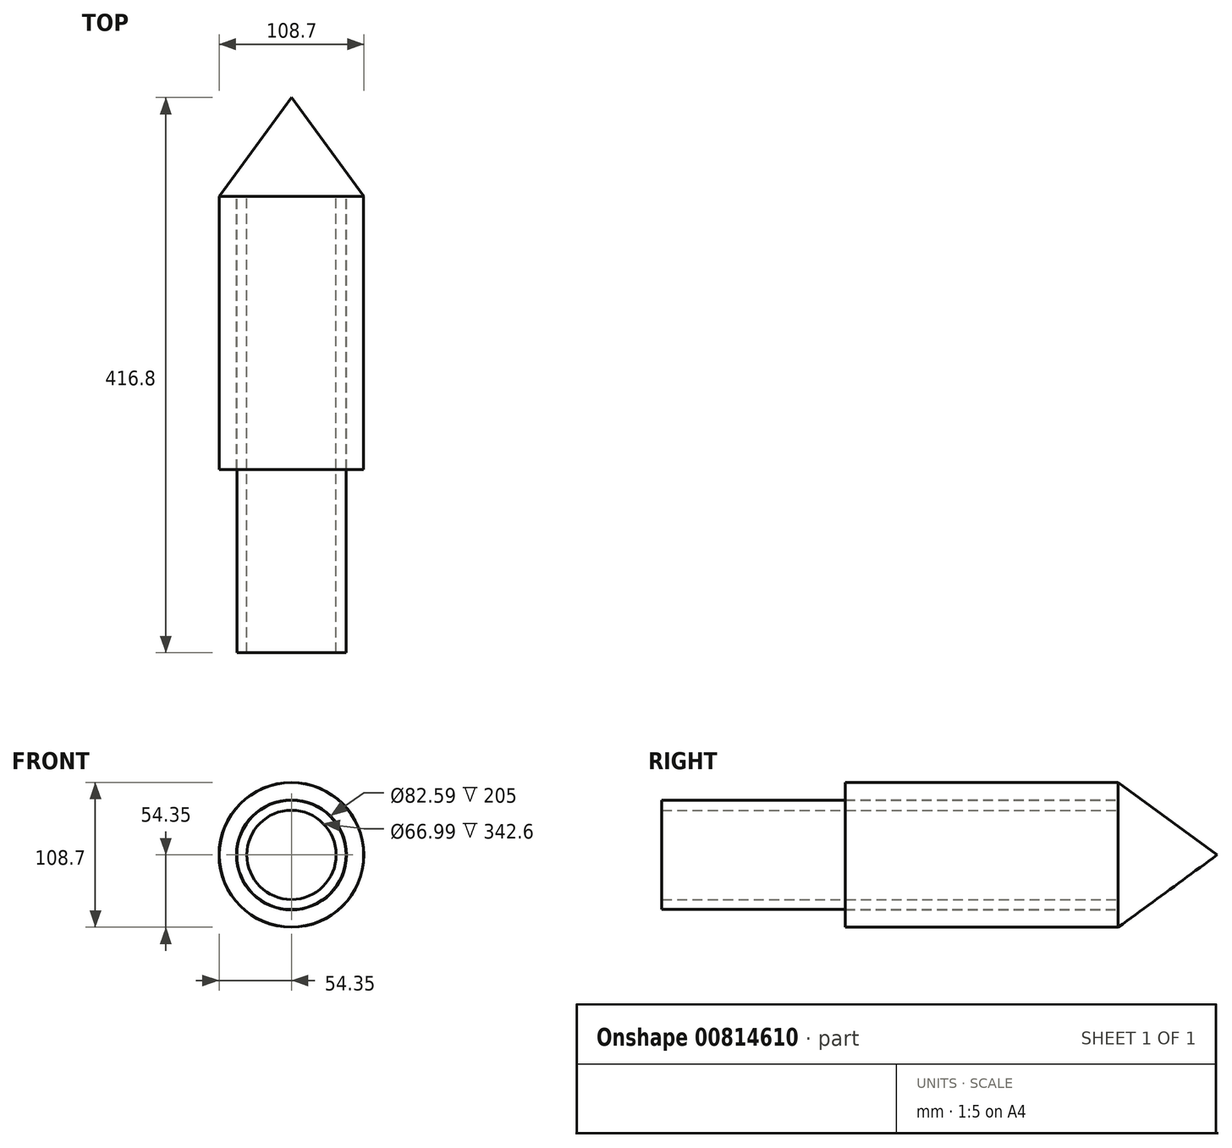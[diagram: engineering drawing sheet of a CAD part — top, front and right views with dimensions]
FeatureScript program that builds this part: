
annotation { "Feature Type Name" : "Feature", "Feature Type Description" : "" }
export const myFeature = defineFeature(function(context is Context, id is Id, definition is map)
    precondition{}
    {
        {
            var Q0;
            Q0=qCreatedBy(makeId("Front.planeOp"),FACE);
            var sketch = newSketch(context, id + "F0", { "sketchPlane" : qUnion([Q0])});
            skCircle(sketch, "E0", {"center": v(0, 0) * mm, "radius": 54.2 * mm});
            skCircle(sketch, "E1", {"center": v(0, 0) * mm, "radius": 41.3 * mm});
            skSolve(sketch);
        }
        {
            var Q0;
            Q0=makeQuery(id+"F0.imprint","IMPRINT",FACE,{"disambiguationData":[TD([[makeQuery(id+"F0.imprint","IMPRINT",EDGE,{"derivedFrom":sQuery(id+"F0.wireOp",EDGE,"E0")}),1.0]])]});
            extrude(context, id + "F1", {"entities" : qUnion([Q0]), "depth" : 205 * mm, "offsetDistance" : 25 * mm});
        }
        {
            var Q0;
            Q0=qCreatedBy(makeId("Right.planeOp"),FACE);
            var sketch = newSketch(context, id + "F2", { "sketchPlane" : qUnion([Q0])});
            skLineSegment(sketch, "E2", {"start": v(0, 0) * mm, "end": v(74.2, 0) * mm});
            skLineSegment(sketch, "E3", {"start": v(0, 0) * mm, "end": v(0, 54.35) * mm});
            skLineSegment(sketch, "E4", {"start": v(0, 54.35) * mm, "end": v(74.2, 0) * mm});
            skSolve(sketch);
        }
        {
            var Q0;
            Q0=makeQuery(id+"F2.imprint","IMPRINT",FACE,{"disambiguationData":[TD([[makeQuery(id+"F2.imprint","IMPRINT",EDGE,{"derivedFrom":sQuery(id+"F2.wireOp",EDGE,"E2")}),1.0]])]});
            var Q1;
            Q1=sQuery(id+"F2.wireOp",EDGE,"E2");
            revolve(context, id + "F3", {"operationType" : NewBodyOperationType.ADD, "surfaceOperationType" : NewSurfaceOperationType.NEW, "entities" : qUnion([Q0]), "axis" : qUnion([Q1]), "revolveType" : RevolveType.FULL});
        }
        {
            var Q0;
            Q0=qCreatedBy(makeId("Front.planeOp"),FACE);
            var sketch = newSketch(context, id + "F4", { "sketchPlane" : qUnion([Q0])});
            skCircle(sketch, "E5", {"center": v(0, 0) * mm, "radius": 41.02 * mm});
            skCircle(sketch, "E6", {"center": v(0, 0) * mm, "radius": 33.5 * mm});
            skSolve(sketch);
        }
        {
            var Q0;
            Q0=makeQuery(id+"F4.imprint","IMPRINT",FACE,{"disambiguationData":[TD([[makeQuery(id+"F4.imprint","IMPRINT",EDGE,{"derivedFrom":sQuery(id+"F4.wireOp",EDGE,"E5")}),1.0]])]});
            extrude(context, id + "F5", {"entities" : qUnion([Q0]), "operationType" : NewBodyOperationType.ADD, "depth" : 342.6 * mm, "offsetDistance" : 25 * mm});
        }
    });
